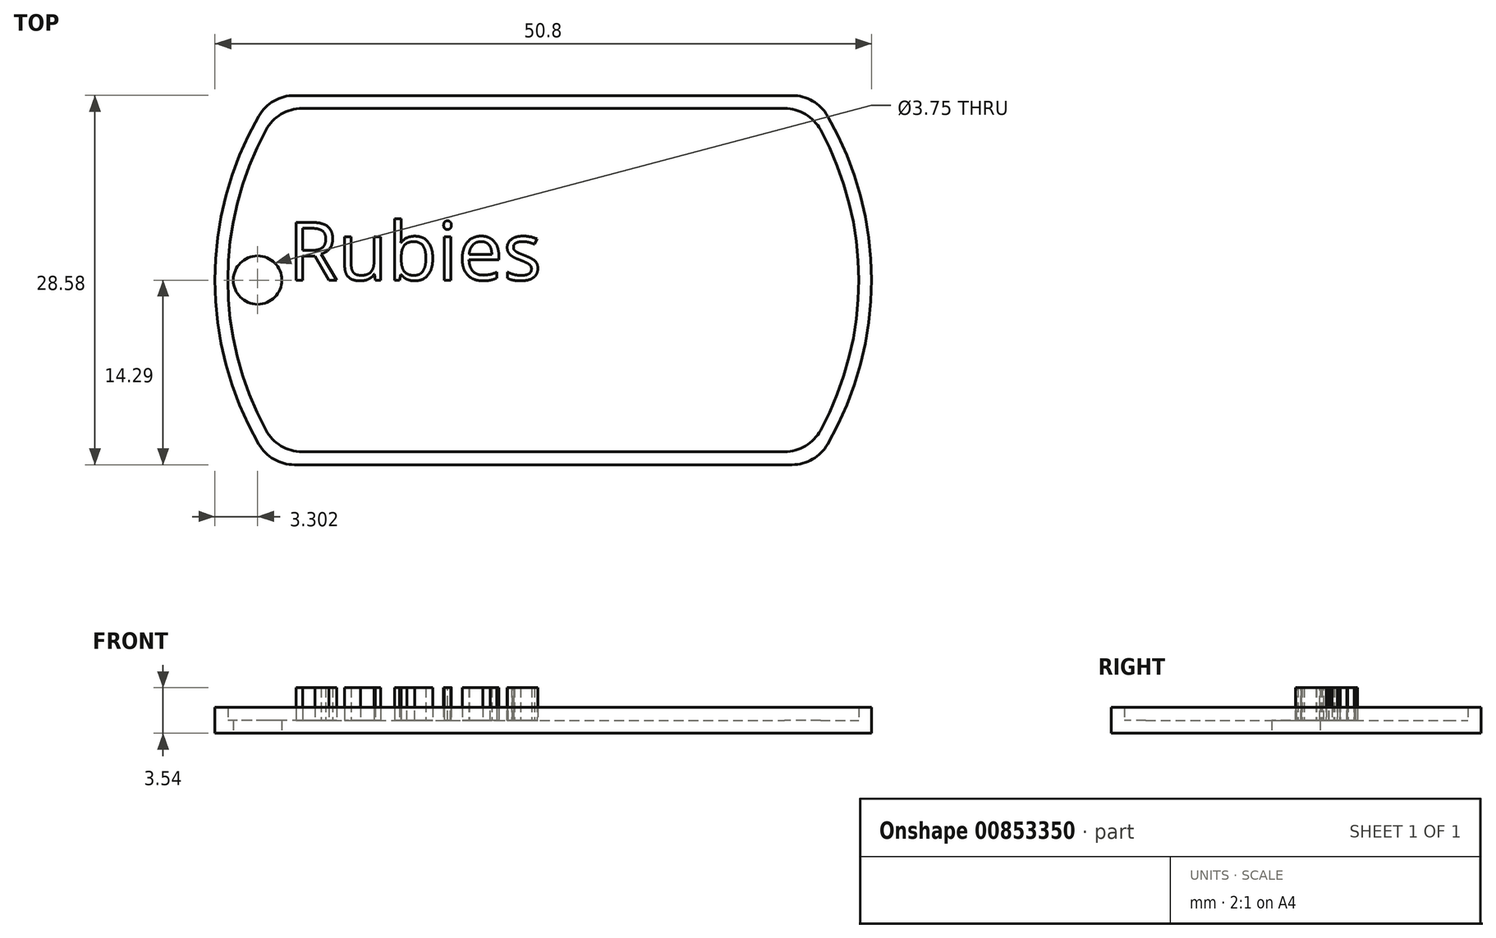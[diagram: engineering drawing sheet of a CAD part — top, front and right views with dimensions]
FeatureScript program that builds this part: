
annotation { "Feature Type Name" : "Feature", "Feature Type Description" : "" }
export const myFeature = defineFeature(function(context is Context, id is Id, definition is map)
    precondition{}
    {
        {
            var Q0;
            Q0=qCreatedBy(makeId("Top.planeOp"),FACE);
            var sketch = newSketch(context, id + "F0", { "sketchPlane" : qUnion([Q0])});
            skArc(sketch, "E0", {"start": v(-22, 12.7) * mm, "mid": v(-25.4, 0) * mm, "end": v(-22, -12.7) * mm});
            skLineSegment(sketch, "E1.top", {"start": v(-19.25, -14.29) * mm, "end": v(19.25, -14.29) * mm});
            skArc(sketch, "E2.trimOffspring", {"start": v(22, -12.7) * mm, "mid": v(25.4, 0) * mm, "end": v(22, 12.7) * mm});
            skLineSegment(sketch, "E3", {"start": v(-19.25, 14.29) * mm, "end": v(19.25, 14.29) * mm});
            skPoint(sketch, "E4.visualSharp", {"position": v(-21, 14.29) * mm});
            skArc(sketch, "E4.filletArc", {"start": v(-19.25, 14.29) * mm, "mid": v(-20.83, 13.86) * mm, "end": v(-22, 12.7) * mm});
            skPoint(sketch, "E5.visualSharp", {"position": v(21, 14.29) * mm});
            skArc(sketch, "E5.filletArc", {"start": v(22, 12.7) * mm, "mid": v(20.83, 13.86) * mm, "end": v(19.25, 14.29) * mm});
            skPoint(sketch, "E6.visualSharp", {"position": v(21, -14.29) * mm});
            skArc(sketch, "E6.filletArc", {"start": v(19.25, -14.29) * mm, "mid": v(20.83, -13.86) * mm, "end": v(22, -12.7) * mm});
            skPoint(sketch, "E7.visualSharp", {"position": v(-21, -14.29) * mm});
            skArc(sketch, "E7.filletArc", {"start": v(-22, -12.7) * mm, "mid": v(-20.83, -13.86) * mm, "end": v(-19.25, -14.29) * mm});
            skCircle(sketch, "E8", {"center": v(-22.1, 0) * mm, "radius": 1.87 * mm});
            skSolve(sketch);
        }
        {
            var Q0;
            Q0=makeQuery(id+"F0.imprint","IMPRINT",FACE,{"disambiguationData":[TD([[makeQuery(id+"F0.imprint","IMPRINT",EDGE,{"derivedFrom":sQuery(id+"F0.wireOp",EDGE,"E0")}),1.0]])]});
            extrude(context, id + "F1", {"entities" : qUnion([Q0]), "depth" : 1 * mm, "offsetDistance" : 25.4 * mm});
        }
        {
            var Q0;
            Q0=makeQuery(id+"F1.opExtrude","CAP_FACE",FACE,{"disambiguationData":[OSD([sQuery(id+"F0.wireOp",EDGE,"E0"),sQuery(id+"F0.wireOp",EDGE,"E1.top"),sQuery(id+"F0.wireOp",EDGE,"E2.trimOffspring"),sQuery(id+"F0.wireOp",EDGE,"E3"),sQuery(id+"F0.wireOp",EDGE,"E4.filletArc"),sQuery(id+"F0.wireOp",EDGE,"E5.filletArc"),sQuery(id+"F0.wireOp",EDGE,"E6.filletArc"),sQuery(id+"F0.wireOp",EDGE,"E7.filletArc")])],"isStart":false});
            var sketch = newSketch(context, id + "F2", { "sketchPlane" : qUnion([Q0])});
            skLineSegment(sketch, "E9.0", {"start": v(-18.66, 13.29) * mm, "end": v(18.66, 13.29) * mm});
            skArc(sketch, "E9.1", {"start": v(-21.45, 11.63) * mm, "mid": v(-24.4, 0) * mm, "end": v(-21.45, -11.63) * mm});
            skLineSegment(sketch, "E9.2", {"start": v(-18.66, -13.29) * mm, "end": v(18.66, -13.29) * mm});
            skArc(sketch, "E9.3", {"start": v(21.45, -11.63) * mm, "mid": v(24.4, 0) * mm, "end": v(21.45, 11.63) * mm});
            skPoint(sketch, "E10.visualSharp", {"position": v(-20.46, 13.29) * mm});
            skArc(sketch, "E10.filletArc", {"start": v(-18.66, 13.29) * mm, "mid": v(-20.29, 12.84) * mm, "end": v(-21.45, 11.63) * mm});
            skPoint(sketch, "E11.visualSharp", {"position": v(20.46, 13.29) * mm});
            skArc(sketch, "E11.filletArc", {"start": v(21.45, 11.63) * mm, "mid": v(20.29, 12.84) * mm, "end": v(18.66, 13.29) * mm});
            skPoint(sketch, "E12.visualSharp", {"position": v(20.46, -13.29) * mm});
            skArc(sketch, "E12.filletArc", {"start": v(18.66, -13.29) * mm, "mid": v(20.29, -12.84) * mm, "end": v(21.45, -11.63) * mm});
            skPoint(sketch, "E13.visualSharp", {"position": v(-20.46, -13.29) * mm});
            skArc(sketch, "E13.filletArc", {"start": v(-21.45, -11.63) * mm, "mid": v(-20.29, -12.84) * mm, "end": v(-18.66, -13.29) * mm});
            skLineSegment(sketch, "E14.0", {"start": v(-19.25, 14.29) * mm, "end": v(19.25, 14.29) * mm});
            skArc(sketch, "E14.1", {"start": v(-22, 12.7) * mm, "mid": v(-25.4, 0) * mm, "end": v(-22, -12.7) * mm});
            skLineSegment(sketch, "E14.2", {"start": v(-19.25, -14.29) * mm, "end": v(19.25, -14.29) * mm});
            skArc(sketch, "E14.3", {"start": v(22, -12.7) * mm, "mid": v(25.4, 0) * mm, "end": v(22, 12.7) * mm});
            skPoint(sketch, "E15.visualSharp", {"position": v(-21, -14.29) * mm});
            skArc(sketch, "E15.filletArc", {"start": v(-22, -12.7) * mm, "mid": v(-20.83, -13.86) * mm, "end": v(-19.25, -14.29) * mm});
            skPoint(sketch, "E16.visualSharp", {"position": v(21, -14.29) * mm});
            skArc(sketch, "E16.filletArc", {"start": v(19.25, -14.29) * mm, "mid": v(20.83, -13.86) * mm, "end": v(22, -12.7) * mm});
            skPoint(sketch, "E17.visualSharp", {"position": v(21, 14.29) * mm});
            skArc(sketch, "E17.filletArc", {"start": v(22, 12.7) * mm, "mid": v(20.83, 13.86) * mm, "end": v(19.25, 14.29) * mm});
            skPoint(sketch, "E18.visualSharp", {"position": v(-21, 14.29) * mm});
            skArc(sketch, "E18.filletArc", {"start": v(-19.25, 14.29) * mm, "mid": v(-20.83, 13.86) * mm, "end": v(-22, 12.7) * mm});
            skSolve(sketch);
        }
        {
            var Q0;
            Q0=makeQuery(id+"F2.imprint","IMPRINT",FACE,{"disambiguationData":[TD([[makeQuery(id+"F2.imprint","IMPRINT",EDGE,{"derivedFrom":sQuery(id+"F2.wireOp",EDGE,"E9.0")}),1.0]])]});
            extrude(context, id + "F3", {"entities" : qUnion([Q0]), "operationType" : NewBodyOperationType.ADD, "depth" : 1 * mm, "offsetDistance" : 25.4 * mm});
        }
        {
            var Q0;
            Q0=makeQuery(id+"F1.opExtrude","CAP_FACE",FACE,{"disambiguationData":[OSD([sQuery(id+"F0.wireOp",EDGE,"E0"),sQuery(id+"F0.wireOp",EDGE,"E1.top"),sQuery(id+"F0.wireOp",EDGE,"E2.trimOffspring"),sQuery(id+"F0.wireOp",EDGE,"E3"),sQuery(id+"F0.wireOp",EDGE,"E4.filletArc"),sQuery(id+"F0.wireOp",EDGE,"E5.filletArc"),sQuery(id+"F0.wireOp",EDGE,"E6.filletArc"),sQuery(id+"F0.wireOp",EDGE,"E7.filletArc"),sQuery(id+"F0.wireOp",EDGE,"E8")])],"isStart":false});
            var sketch = newSketch(context, id + "F4", { "sketchPlane" : qUnion([Q0])});
            skText(sketch, "E19", { "text": "Rubies", "fontName": "OpenSans-Regular.ttf"});
            const initialGuessF4  = {"E19": [-0.01973, 0, 1, 0, 0.0045]};
            skSetInitialGuess(sketch, initialGuessF4);
            skSolve(sketch);
        }
        {
            var Q0;
            Q0 = qSketchRegion(id + "F4", true);
            extrude(context, id + "F5", {"entities" : qUnion([Q0]), "operationType" : NewBodyOperationType.ADD, "depth" : 2.54 * mm, "offsetDistance" : 25.4 * mm});
        }
    });
